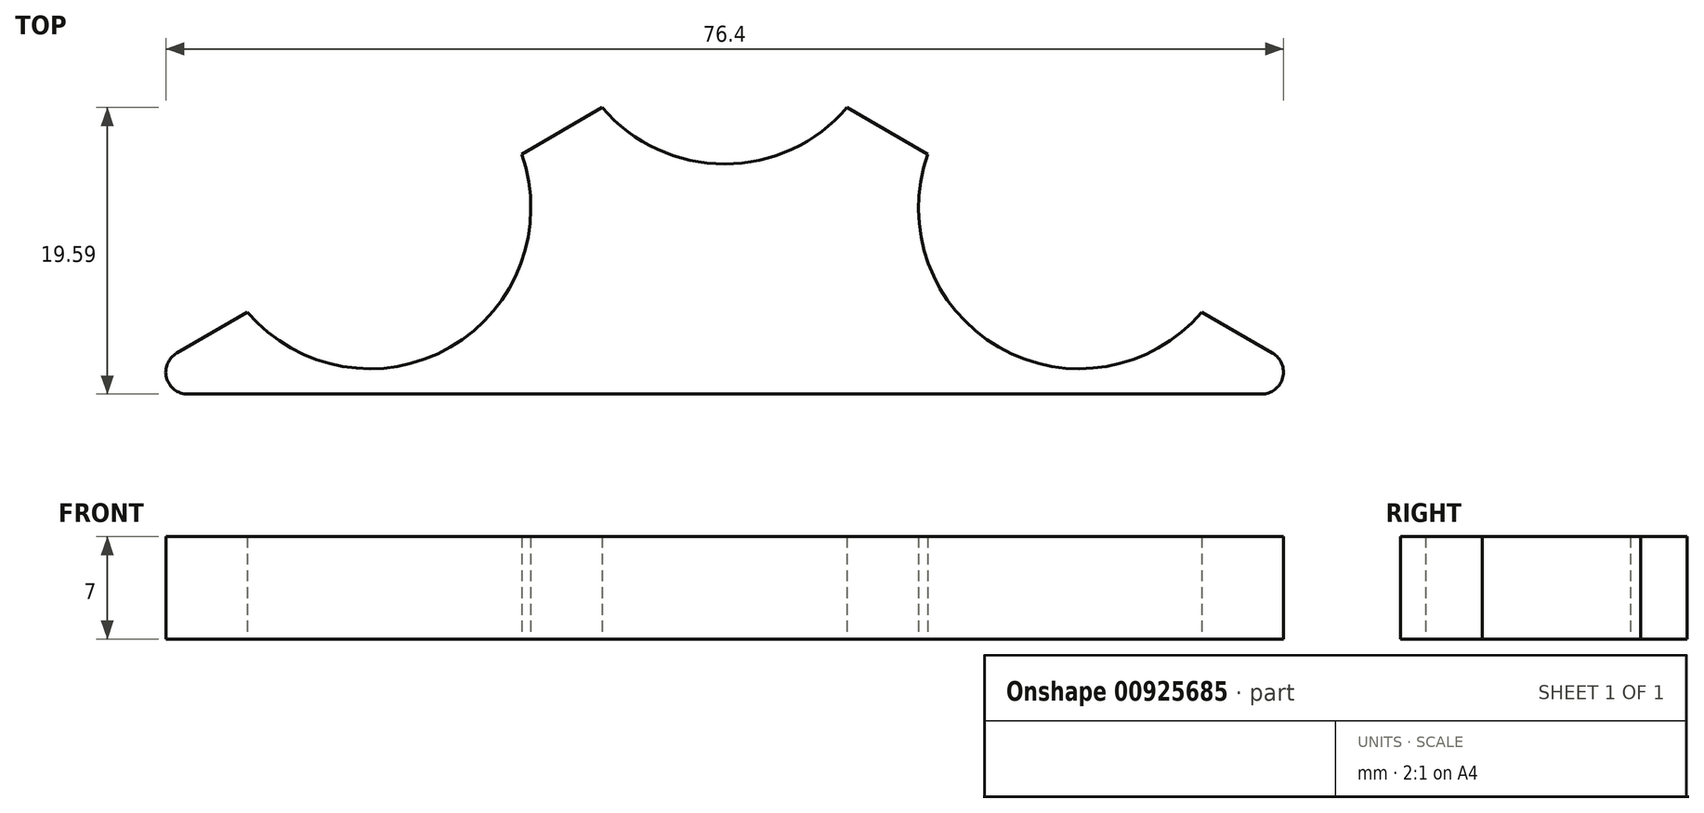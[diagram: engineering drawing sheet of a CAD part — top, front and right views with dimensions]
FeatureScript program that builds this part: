
annotation { "Feature Type Name" : "Feature", "Feature Type Description" : "" }
export const myFeature = defineFeature(function(context is Context, id is Id, definition is map)
    precondition{}
    {
        {
            var Q0;
            Q0=qCreatedBy(makeId("Top.planeOp"),FACE);
            var sketch = newSketch(context, id + "F0", { "sketchPlane" : qUnion([Q0])});
            skCircle(sketch, "E0", {"center": v(0, 0) * mm, "radius": 50 * mm, "construction": true});
            skLineSegment(sketch, "E1", {"start": v(0, 50) * mm, "end": v(0, 0) * mm, "construction": true});
            skLineSegment(sketch, "E2", {"start": v(0, 0) * mm, "end": v(43.3, -25) * mm, "construction": true});
            skLineSegment(sketch, "E3.MirrorCS", {"start": v(0, 0) * mm, "end": v(-43.3, -25) * mm, "construction": true});
            skCircle(sketch, "E4", {"center": v(0, 0) * mm, "radius": 11 * mm});
            skCircle(sketch, "E5", {"center": v(-24.25, -14) * mm, "radius": 11 * mm});
            skLineSegment(sketch, "E6.0", {"start": v(0, -2.3) * mm, "end": v(42.3, -26.73) * mm});
            skLineSegment(sketch, "E6.1", {"start": v(0, -2.3) * mm, "end": v(-42.3, -26.73) * mm});
            skLineSegment(sketch, "E7", {"start": v(-42.3, -26.73) * mm, "end": v(42.3, -26.73) * mm});
            skCircle(sketch, "E8.MirrorC", {"center": v(24.25, -14) * mm, "radius": 11 * mm});
            skSolve(sketch);
        }
        {
            var Q0;
            {var subQ0=sQuery(id+"F0.wireOp",EDGE,"E7");Q0=makeQuery(id+"F0.imprint","IMPRINT",FACE,{"disambiguationData":[TD([[makeQuery(id+"F0.imprint","IMPRINT",EDGE,{"derivedFrom":subQ0}),1.0]])]});}
            extrude(context, id + "F1", {"entities" : qUnion([Q0]), "depth" : 7 * mm, "offsetDistance" : 25 * mm});
        }
        {
            var Q0;
            Q0=makeQuery(id+"F1.opExtrude","SWEPT_EDGE",EDGE,{"disambiguationData":[OSD([sQuery(id+"F0.wireOp",EDGE,"E6.1"),sQuery(id+"F0.wireOp",EDGE,"E7")])]});
            var Q1;
            Q1=makeQuery(id+"F1.opExtrude","SWEPT_EDGE",EDGE,{"disambiguationData":[OSD([sQuery(id+"F0.wireOp",EDGE,"E6.0"),sQuery(id+"F0.wireOp",EDGE,"E7")])]});
            fillet(context, id + "F2", {"entities" : qUnion([Q0, Q1]), "radius" : 1.5 * mm, "tangentPropagation" : true, "allowEdgeOverflow" : false});
        }
    });
